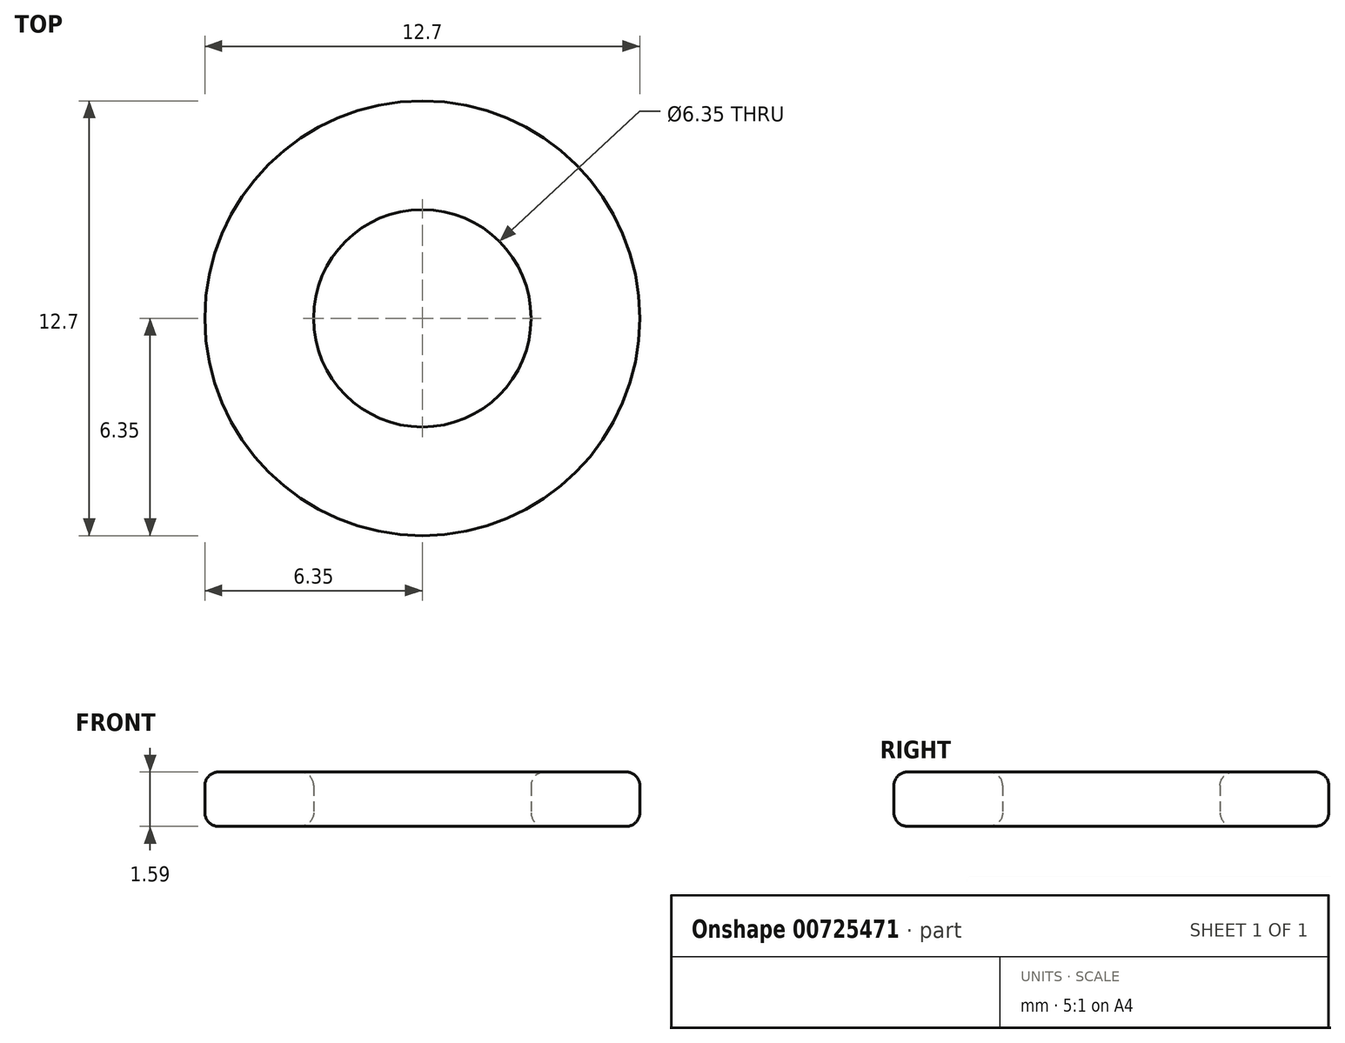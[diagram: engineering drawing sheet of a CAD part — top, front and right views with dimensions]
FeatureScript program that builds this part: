
annotation { "Feature Type Name" : "Feature", "Feature Type Description" : "" }
export const myFeature = defineFeature(function(context is Context, id is Id, definition is map)
    precondition{}
    {
        {
            var Q0;
            Q0=qCreatedBy(makeId("Top.planeOp"),FACE);
            var sketch = newSketch(context, id + "F0", { "sketchPlane" : qUnion([Q0])});
            skCircle(sketch, "E0", {"center": v(0, 0) * mm, "radius": 3.18 * mm});
            skCircle(sketch, "E1", {"center": v(0, 0) * mm, "radius": 6.35 * mm});
            skSolve(sketch);
        }
        {
            var Q0;
            Q0=makeQuery(id+"F0.imprint","IMPRINT",FACE,{"disambiguationData":[TD([[makeQuery(id+"F0.imprint","IMPRINT",EDGE,{"derivedFrom":sQuery(id+"F0.wireOp",EDGE,"E0")}),-1.0]])]});
            extrude(context, id + "F1", {"entities" : qUnion([Q0]), "depth" : 1.59 * mm, "offsetDistance" : 25.4 * mm});
        }
        {
            var Q0;
            Q0=makeQuery(id+"F1.opExtrude","CAP_EDGE",EDGE,{"disambiguationData":[OSD([sQuery(id+"F0.wireOp",EDGE,"E1")])],"isStart":true});
            var Q1;
            Q1=makeQuery(id+"F1.opExtrude","CAP_FACE",FACE,{"disambiguationData":[OSD([sQuery(id+"F0.wireOp",EDGE,"E0"),sQuery(id+"F0.wireOp",EDGE,"E1")])],"isStart":true});
            var Q2;
            Q2=makeQuery(id+"F1.opExtrude","CAP_EDGE",EDGE,{"disambiguationData":[OSD([sQuery(id+"F0.wireOp",EDGE,"E0")])],"isStart":false});
            var Q3;
            Q3=makeQuery(id+"F1.opExtrude","SWEPT_FACE",FACE,{"disambiguationData":[OSD([sQuery(id+"F0.wireOp",EDGE,"E0")])]});
            var Q4;
            Q4=makeQuery(id+"F1.opExtrude","CAP_FACE",FACE,{"disambiguationData":[OSD([sQuery(id+"F0.wireOp",EDGE,"E0"),sQuery(id+"F0.wireOp",EDGE,"E1")])],"isStart":false});
            var Q5;
            Q5=makeQuery(id+"F1.opExtrude","CAP_EDGE",EDGE,{"disambiguationData":[OSD([sQuery(id+"F0.wireOp",EDGE,"E1")])],"isStart":false});
            var Q6;
            Q6=makeQuery(id+"F1.opExtrude","SWEPT_FACE",FACE,{"disambiguationData":[OSD([sQuery(id+"F0.wireOp",EDGE,"E1")])]});
            var Q7;
            Q7=makeQuery(id+"F1.opExtrude","CAP_EDGE",EDGE,{"disambiguationData":[OSD([sQuery(id+"F0.wireOp",EDGE,"E0")])],"isStart":true});
            fillet(context, id + "F2", {"entities" : qUnion([Q0, Q1, Q2, Q3, Q4, Q5, Q6, Q7]), "radius" : 0.4 * mm, "tangentPropagation" : true, "allowEdgeOverflow" : false});
        }
    });
